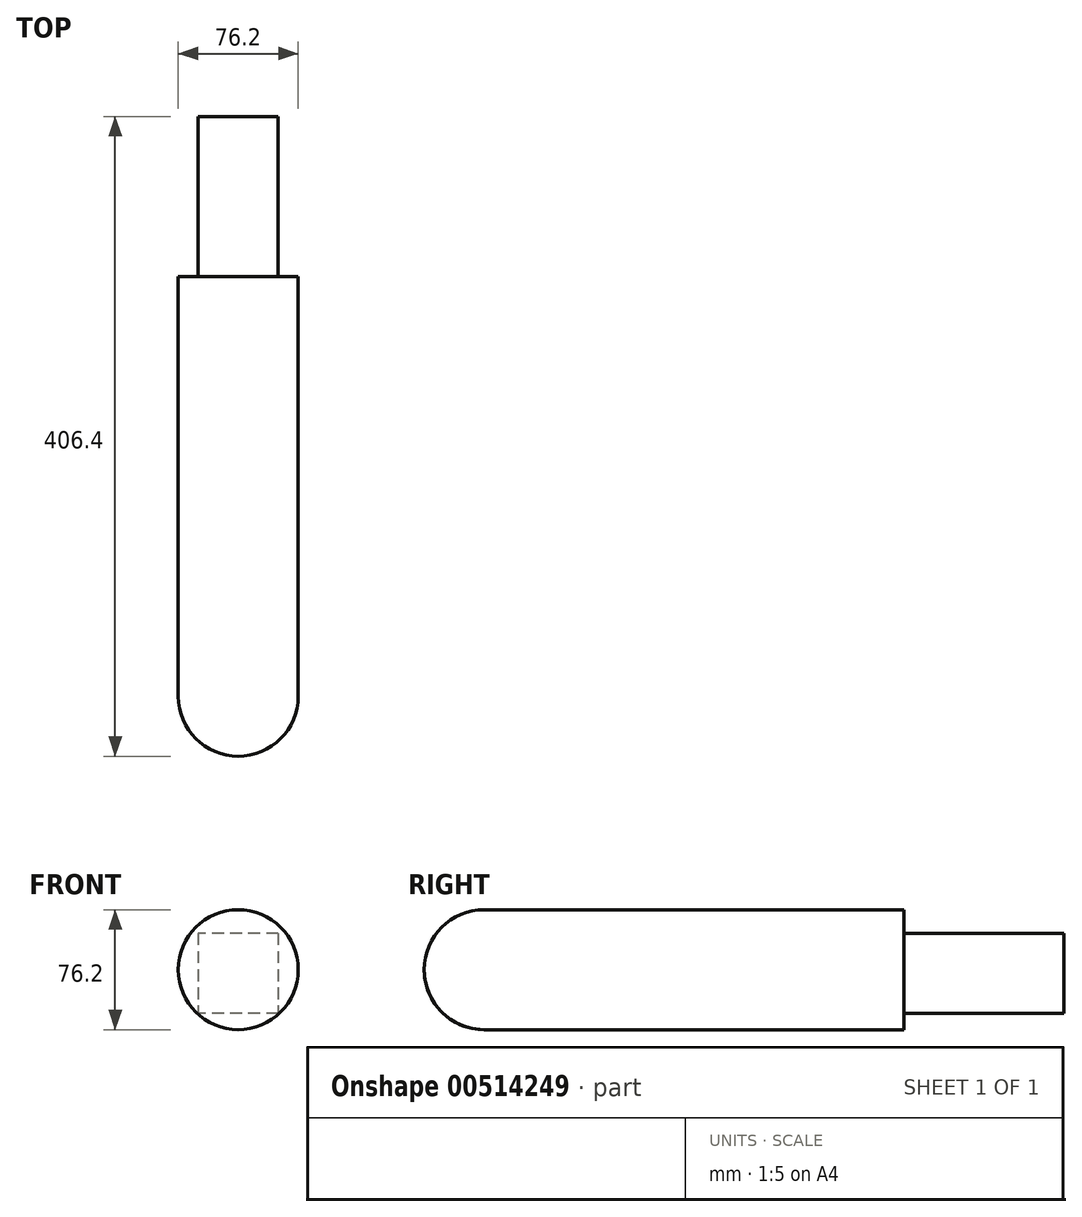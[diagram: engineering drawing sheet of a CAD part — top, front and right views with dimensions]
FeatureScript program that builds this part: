
annotation { "Feature Type Name" : "Feature", "Feature Type Description" : "" }
export const myFeature = defineFeature(function(context is Context, id is Id, definition is map)
    precondition{}
    {
        {
            var Q0;
            Q0=qCreatedBy(makeId("Front.planeOp"),FACE);
            var sketch = newSketch(context, id + "F0", { "sketchPlane" : qUnion([Q0])});
            skLineSegment(sketch, "E0.bottom", {"start": v(25.4, 25.4) * mm, "end": v(-25.4, 25.4) * mm});
            skLineSegment(sketch, "E0.top", {"start": v(25.4, -25.4) * mm, "end": v(-25.4, -25.4) * mm});
            skLineSegment(sketch, "E0.left", {"start": v(25.4, 25.4) * mm, "end": v(25.4, -25.4) * mm});
            skLineSegment(sketch, "E0.right", {"start": v(-25.4, 25.4) * mm, "end": v(-25.4, -25.4) * mm});
            skPoint(sketch, "E0.middle", {"position": v(0, 0) * mm});
            skSolve(sketch);
        }
        {
            var Q0;
            Q0=makeQuery(id+"F0.imprint","IMPRINT",FACE,{"disambiguationData":[TD([[makeQuery(id+"F0.imprint","IMPRINT",EDGE,{"derivedFrom":sQuery(id+"F0.wireOp",EDGE,"E0.bottom")}),1.0]])]});
            extrude(context, id + "F1", {"entities" : qUnion([Q0]), "depth" : 101.6 * mm, "offsetDistance" : 25.4 * mm});
        }
        {
            var Q0;
            Q0=makeQuery(id+"F1.opExtrude","CAP_FACE",FACE,{"disambiguationData":[OSD([sQuery(id+"F0.wireOp",EDGE,"E0.bottom"),sQuery(id+"F0.wireOp",EDGE,"E0.top"),sQuery(id+"F0.wireOp",EDGE,"E0.left"),sQuery(id+"F0.wireOp",EDGE,"E0.right")])],"isStart":false});
            var sketch = newSketch(context, id + "F2", { "sketchPlane" : qUnion([Q0])});
            skCircle(sketch, "E1", {"center": v(0, 2.22) * mm, "radius": 38.1 * mm});
            skSolve(sketch);
        }
        {
            var Q0;
            Q0 = qSketchRegion(id + "F2", true);
            extrude(context, id + "F3", {"entities" : qUnion([Q0]), "operationType" : NewBodyOperationType.ADD, "depth" : 304.8 * mm, "offsetDistance" : 25.4 * mm});
        }
        {
            var Q0;
            Q0=makeQuery(id+"F3.opExtrude","CAP_FACE",FACE,{"disambiguationData":[OSD([sQuery(id+"F2.wireOp",EDGE,"E1")])],"isStart":false});
            fillet(context, id + "F4", {"entities" : qUnion([Q0]), "radius" : 38.1 * mm, "tangentPropagation" : true, "allowEdgeOverflow" : false});
        }
    });
